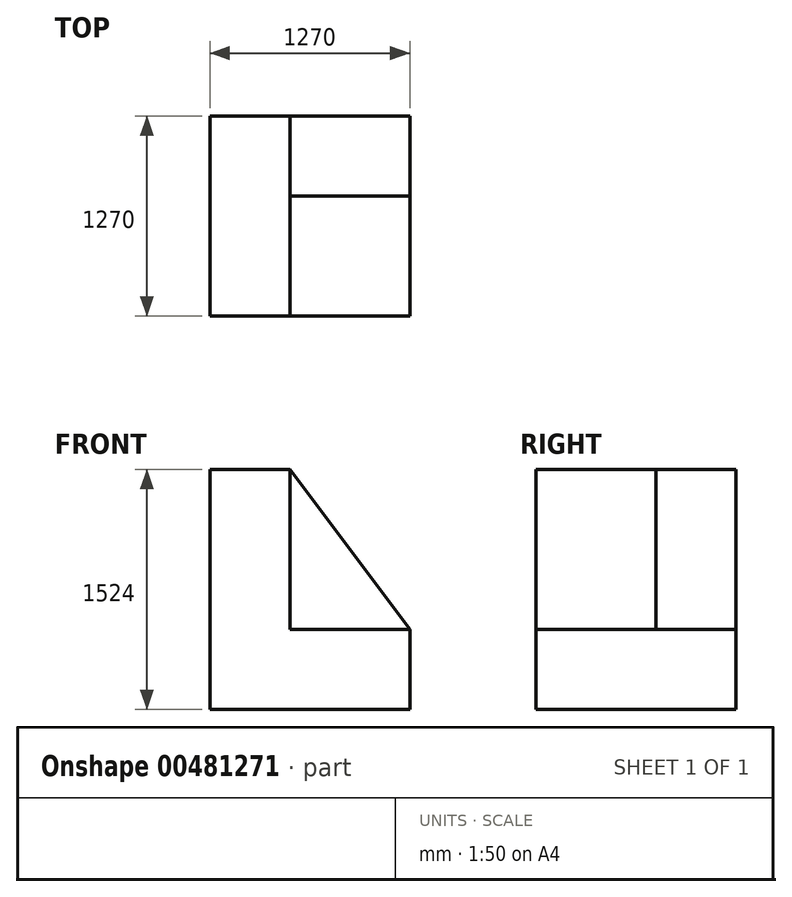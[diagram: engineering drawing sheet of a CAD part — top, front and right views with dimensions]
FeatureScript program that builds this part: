
annotation { "Feature Type Name" : "Feature", "Feature Type Description" : "" }
export const myFeature = defineFeature(function(context is Context, id is Id, definition is map)
    precondition{}
    {
        {
            var Q0;
            Q0=qCreatedBy(makeId("Front.planeOp"),FACE);
            var sketch = newSketch(context, id + "F0", { "sketchPlane" : qUnion([Q0])});
            skLineSegment(sketch, "E0", {"start": v(0, 0) * mm, "end": v(1270, 0) * mm});
            skLineSegment(sketch, "E1", {"start": v(1270, 0) * mm, "end": v(1270, 508) * mm});
            skLineSegment(sketch, "E2", {"start": v(1270, 508) * mm, "end": v(508, 508) * mm});
            skLineSegment(sketch, "E3", {"start": v(508, 508) * mm, "end": v(508, 1524) * mm});
            skLineSegment(sketch, "E4", {"start": v(508, 1524) * mm, "end": v(0, 1524) * mm});
            skLineSegment(sketch, "E5", {"start": v(0, 1524) * mm, "end": v(0, 0) * mm});
            skLineSegment(sketch, "E6", {"start": v(508, 1524) * mm, "end": v(1270, 508) * mm});
            skSolve(sketch);
        }
        {
            var Q0;
            Q0=makeQuery(id+"F0.imprint","IMPRINT",FACE,{"disambiguationData":[TD([[makeQuery(id+"F0.imprint","IMPRINT",EDGE,{"derivedFrom":sQuery(id+"F0.wireOp",EDGE,"E0")}),1.0]])]});
            extrude(context, id + "F1", {"entities" : qUnion([Q0]), "depth" : 1270 * mm});
        }
        {
            var Q0;
            Q0 = qSketchRegion(id + "F0", true);
            extrude(context, id + "F2", {"entities" : qUnion([Q0]), "operationType" : NewBodyOperationType.ADD, "depth" : 508 * mm});
        }
    });
